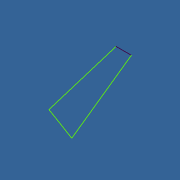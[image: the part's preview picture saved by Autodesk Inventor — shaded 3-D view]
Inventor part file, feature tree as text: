
AUTODESK INVENTOR PART (.ipt)
format: ipt  version: 2018 (Build 220112000, 112)  size: 70,144 bytes
history: native  units: mm
features: extrude x1, sketch x1
ambient origin geometry x8: Origin, YZ Plane, XZ Plane, XY Plane, X Axis, Y Axis, Z Axis, Center Point
bodies: Solid1 (feature_tree)
feature tree (2):
  extrude  "Extrusion1"  [1 undecoded]
  sketch  "Sketch1"  dims[d0=1.0mm d1=0.0mm]
note: 1 required parameter value undecoded (feature->parameter linkage not recoverable at this tier; creation-order binding heuristic only, values carry confidence <= 0.55)
